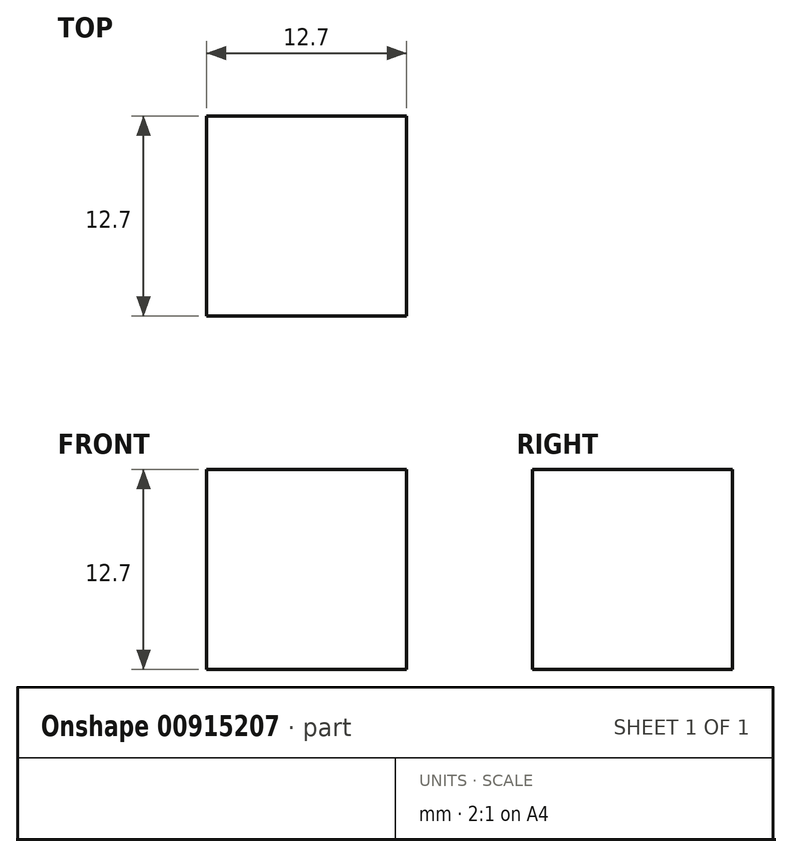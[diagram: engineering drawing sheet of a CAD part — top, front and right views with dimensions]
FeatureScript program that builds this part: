
annotation { "Feature Type Name" : "Feature", "Feature Type Description" : "" }
export const myFeature = defineFeature(function(context is Context, id is Id, definition is map)
    precondition{}
    {
        {
            var Q0;
            Q0=qCreatedBy(makeId("Front.planeOp"),FACE);
            var sketch = newSketch(context, id + "F0", { "sketchPlane" : qUnion([Q0])});
            skLineSegment(sketch, "E0.bottom", {"start": v(-5.85, 8.8) * mm, "end": v(6.85, 8.8) * mm});
            skLineSegment(sketch, "E0.top", {"start": v(-5.85, -3.9) * mm, "end": v(6.85, -3.9) * mm});
            skLineSegment(sketch, "E0.left", {"start": v(-5.85, 8.8) * mm, "end": v(-5.85, -3.9) * mm});
            skLineSegment(sketch, "E0.right", {"start": v(6.85, 8.8) * mm, "end": v(6.85, -3.9) * mm});
            skSolve(sketch);
        }
        {
            var Q0;
            Q0 = qSketchRegion(id + "F0", true);
            extrude(context, id + "F1", {"entities" : qUnion([Q0]), "depth" : 12.7 * mm, "offsetDistance" : 25.4 * mm});
        }
    });
